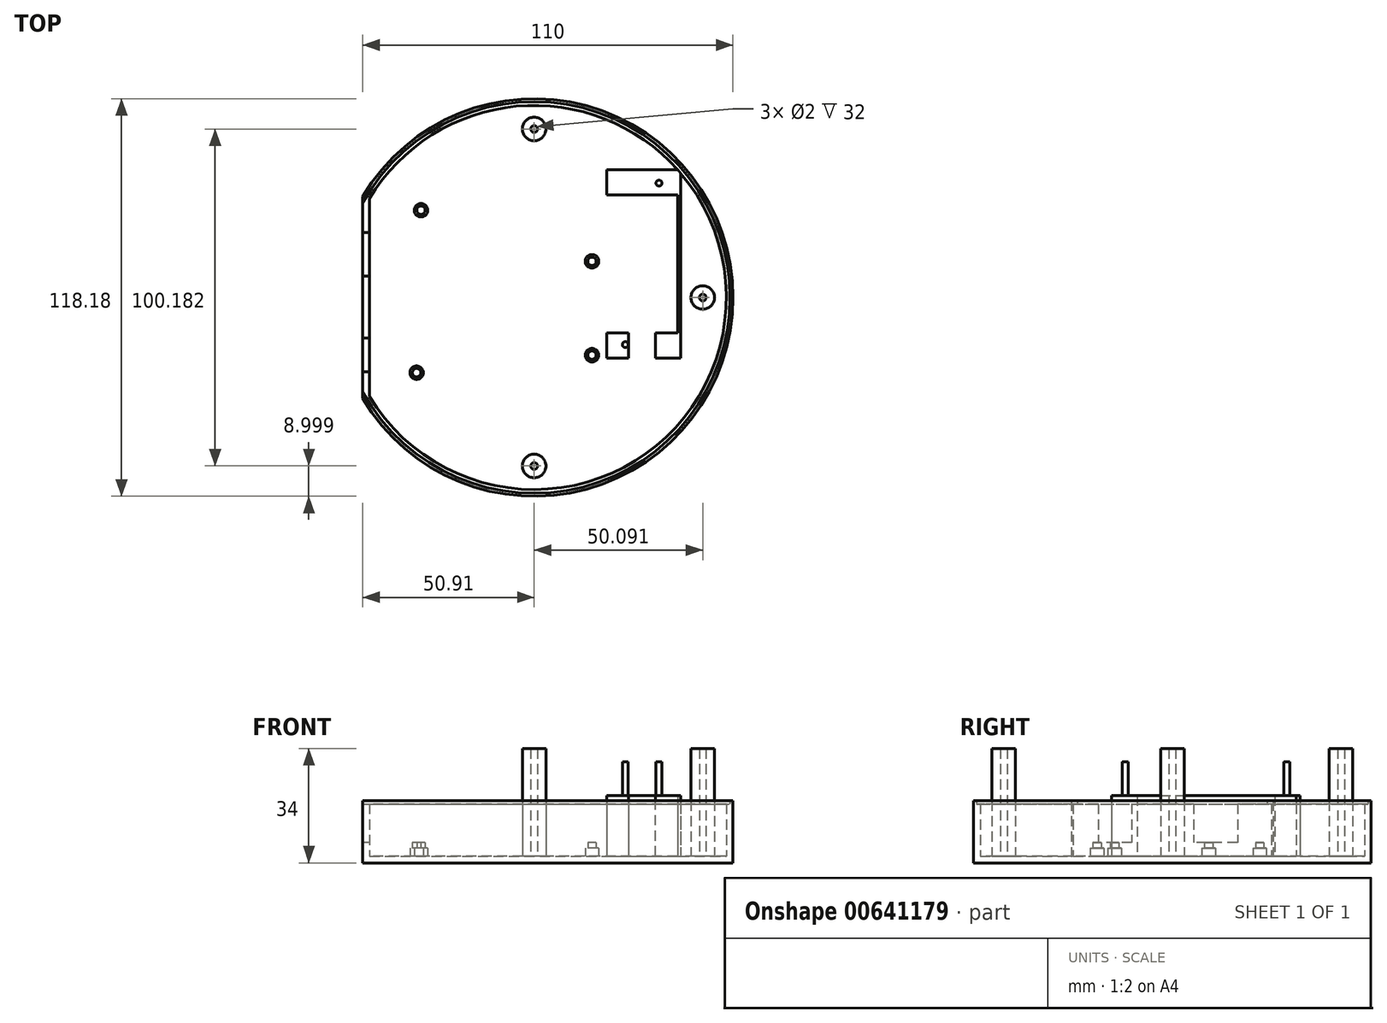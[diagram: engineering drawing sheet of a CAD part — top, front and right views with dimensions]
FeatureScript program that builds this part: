
annotation { "Feature Type Name" : "Feature", "Feature Type Description" : "" }
export const myFeature = defineFeature(function(context is Context, id is Id, definition is map)
    precondition{}
    {
        {
            var Q0;
            Q0=qCreatedBy(makeId("Top.planeOp"),FACE);
            var sketch = newSketch(context, id + "F0", { "sketchPlane" : qUnion([Q0])});
            skArc(sketch, "E0", {"start": v(-50.9, -30) * mm, "mid": v(59.1, 0) * mm, "end": v(-50.9, 30) * mm});
            skLineSegment(sketch, "E1", {"start": v(-50.9, 30) * mm, "end": v(-50.9, -30) * mm});
            skSolve(sketch);
        }
        {
            var Q0;
            Q0=makeQuery(id+"F0.imprint","IMPRINT",FACE,{"disambiguationData":[TD([[makeQuery(id+"F0.imprint","IMPRINT",EDGE,{"derivedFrom":sQuery(id+"F0.wireOp",EDGE,"E0")}),1.0]])]});
            extrude(context, id + "F1", {"entities" : qUnion([Q0]), "depth" : 2 * mm, "offsetDistance" : 25 * mm});
        }
        {
            var Q0;
            Q0=makeQuery(id+"F1.opExtrude","CAP_FACE",FACE,{"disambiguationData":[OSD([sQuery(id+"F0.wireOp",EDGE,"E0"),sQuery(id+"F0.wireOp",EDGE,"E1")])],"isStart":false});
            var sketch = newSketch(context, id + "F2", { "sketchPlane" : qUnion([Q0])});
            skArc(sketch, "E2", {"start": v(-48.9, -29.45) * mm, "mid": v(57.1, 0) * mm, "end": v(-48.9, 29.45) * mm});
            skLineSegment(sketch, "E3", {"start": v(-48.9, 29.45) * mm, "end": v(-48.9, -29.45) * mm});
            skLineSegment(sketch, "E4.bottom", {"start": v(-48.9, -24.85) * mm, "end": v(19.6, -24.85) * mm, "construction": true});
            skLineSegment(sketch, "E4.top", {"start": v(-48.9, 28.45) * mm, "end": v(19.6, 28.45) * mm, "construction": true});
            skLineSegment(sketch, "E4.left", {"start": v(-48.9, -24.85) * mm, "end": v(-48.9, 28.45) * mm, "construction": true});
            skLineSegment(sketch, "E4.right", {"start": v(19.6, -24.85) * mm, "end": v(19.6, 28.45) * mm, "construction": true});
            skLineSegment(sketch, "E5", {"start": v(-50.9, 19.35) * mm, "end": v(-48.9, 19.35) * mm});
            skLineSegment(sketch, "E6", {"start": v(-50.9, 6.35) * mm, "end": v(-48.9, 6.35) * mm});
            skLineSegment(sketch, "E7", {"start": v(-50.9, -12.05) * mm, "end": v(-48.9, -12.05) * mm});
            skLineSegment(sketch, "E8", {"start": v(-50.9, -22.05) * mm, "end": v(-48.9, -22.05) * mm});
            skCircle(sketch, "E9", {"center": v(-34.9, -22.35) * mm, "radius": 2 * mm});
            skCircle(sketch, "E10", {"center": v(-33.6, 25.95) * mm, "radius": 2 * mm});
            skCircle(sketch, "E11", {"center": v(17.2, 10.75) * mm, "radius": 2 * mm});
            skLineSegment(sketch, "E12", {"start": v(17.2, 10.75) * mm, "end": v(17.2, -19.32) * mm, "construction": true});
            skCircle(sketch, "E13", {"center": v(17.2, -17.15) * mm, "radius": 2 * mm});
            skCircle(sketch, "E14", {"center": v(-33.6, 25.95) * mm, "radius": 1.25 * mm});
            skCircle(sketch, "E15", {"center": v(-34.9, -22.35) * mm, "radius": 1.25 * mm});
            skCircle(sketch, "E16", {"center": v(17.2, 10.75) * mm, "radius": 1.25 * mm});
            skCircle(sketch, "E17", {"center": v(17.2, -17.15) * mm, "radius": 1.25 * mm});
            skSolve(sketch);
        }
        {
            var Q0;
            {var subQ2=sQuery(id+"F2.wireOp",EDGE,"E2");Q0=makeQuery(id+"F2.imprint","IMPRINT",FACE,{"disambiguationData":[TD([[makeQuery(id+"F2.imprint","IMPRINT",EDGE,{"derivedFrom":subQ2}),-1.0]])]});}
            var Q1;
            {var subQ0=sQuery(id+"F2.wireOp",EDGE,"E6");Q1=makeQuery(id+"F2.imprint","IMPRINT",FACE,{"disambiguationData":[TD([[makeQuery(id+"F2.imprint","IMPRINT",EDGE,{"derivedFrom":subQ0}),-1.0]])]});}
            var Q2;
            {var subQ0=sQuery(id+"F2.wireOp",EDGE,"E5");Q2=makeQuery(id+"F2.imprint","IMPRINT",FACE,{"disambiguationData":[TD([[makeQuery(id+"F2.imprint","IMPRINT",EDGE,{"derivedFrom":subQ0}),-1.0]])]});}
            var Q3;
            {var subQ0=sQuery(id+"F2.wireOp",EDGE,"E7");Q3=makeQuery(id+"F2.imprint","IMPRINT",FACE,{"disambiguationData":[TD([[makeQuery(id+"F2.imprint","IMPRINT",EDGE,{"derivedFrom":subQ0}),-1.0]])]});}
            extrude(context, id + "F3", {"entities" : qUnion([Q0, Q1, Q2, Q3]), "operationType" : NewBodyOperationType.ADD, "depth" : 4 * mm, "offsetDistance" : 25 * mm});
        }
        {
            var Q0;
            Q0=makeQuery(id+"F2.imprint","IMPRINT",FACE,{"disambiguationData":[TD([[makeQuery(id+"F2.imprint","IMPRINT",EDGE,{"derivedFrom":sQuery(id+"F2.wireOp",EDGE,"E14")}),1.0]])]});
            var Q1;
            Q1=makeQuery(id+"F2.imprint","IMPRINT",FACE,{"disambiguationData":[TD([[makeQuery(id+"F2.imprint","IMPRINT",EDGE,{"derivedFrom":sQuery(id+"F2.wireOp",EDGE,"E15")}),1.0]])]});
            var Q2;
            Q2=makeQuery(id+"F2.imprint","IMPRINT",FACE,{"disambiguationData":[TD([[makeQuery(id+"F2.imprint","IMPRINT",EDGE,{"derivedFrom":sQuery(id+"F2.wireOp",EDGE,"E16")}),1.0]])]});
            var Q3;
            Q3=makeQuery(id+"F2.imprint","IMPRINT",FACE,{"disambiguationData":[TD([[makeQuery(id+"F2.imprint","IMPRINT",EDGE,{"derivedFrom":sQuery(id+"F2.wireOp",EDGE,"E17")}),1.0]])]});
            extrude(context, id + "F4", {"entities" : qUnion([Q0, Q1, Q2, Q3]), "operationType" : NewBodyOperationType.ADD, "depth" : 4 * mm, "offsetDistance" : 25 * mm});
        }
        {
            var Q0;
            Q0=makeQuery(id+"F2.imprint","IMPRINT",FACE,{"disambiguationData":[TD([[makeQuery(id+"F2.imprint","IMPRINT",EDGE,{"derivedFrom":sQuery(id+"F2.wireOp",EDGE,"E10")}),1.0]])]});
            var Q1;
            Q1=makeQuery(id+"F2.imprint","IMPRINT",FACE,{"disambiguationData":[TD([[makeQuery(id+"F2.imprint","IMPRINT",EDGE,{"derivedFrom":sQuery(id+"F2.wireOp",EDGE,"E9")}),1.0]])]});
            var Q2;
            Q2=makeQuery(id+"F2.imprint","IMPRINT",FACE,{"disambiguationData":[TD([[makeQuery(id+"F2.imprint","IMPRINT",EDGE,{"derivedFrom":sQuery(id+"F2.wireOp",EDGE,"E13")}),1.0]])]});
            var Q3;
            Q3=makeQuery(id+"F2.imprint","IMPRINT",FACE,{"disambiguationData":[TD([[makeQuery(id+"F2.imprint","IMPRINT",EDGE,{"derivedFrom":sQuery(id+"F2.wireOp",EDGE,"E11")}),1.0]])]});
            extrude(context, id + "F5", {"entities" : qUnion([Q0, Q1, Q2, Q3]), "operationType" : NewBodyOperationType.ADD, "depth" : 2.4 * mm, "offsetDistance" : 25 * mm});
        }
        {
            var Q0;
            {var subQ2=sQuery(id+"F2.wireOp",EDGE,"E2");Q0=makeQuery(id+"F2.imprint","IMPRINT",FACE,{"disambiguationData":[TD([[makeQuery(id+"F2.imprint","IMPRINT",EDGE,{"derivedFrom":subQ2}),-1.0]])]});}
            var Q1;
            {var subQ0=sQuery(id+"F2.wireOp",EDGE,"E6");Q1=makeQuery(id+"F2.imprint","IMPRINT",FACE,{"disambiguationData":[TD([[makeQuery(id+"F2.imprint","IMPRINT",EDGE,{"derivedFrom":subQ0}),-1.0]])]});}
            extrude(context, id + "F6", {"entities" : qUnion([Q0, Q1]), "operationType" : NewBodyOperationType.ADD, "depth" : 15.5 * mm, "offsetDistance" : 25 * mm});
        }
        {
            var Q0;
            {var subQ4=sQuery(id+"F2.wireOp",EDGE,"E2");Q0=makeQuery(id+"F2.imprint","IMPRINT",FACE,{"disambiguationData":[TD([[makeQuery(id+"F2.imprint","IMPRINT",EDGE,{"derivedFrom":subQ4}),1.0]])]});}
            var sketch = newSketch(context, id + "F7", { "sketchPlane" : qUnion([Q0])});
            skCircle(sketch, "E18", {"center": v(50.1, 0) * mm, "radius": 3.5 * mm});
            skCircle(sketch, "E19", {"center": v(0, 50.1) * mm, "radius": 3.5 * mm});
            skCircle(sketch, "E20", {"center": v(0, -50.1) * mm, "radius": 3.5 * mm});
            skCircle(sketch, "E21", {"center": v(0, -50.1) * mm, "radius": 1 * mm});
            skCircle(sketch, "E22", {"center": v(0, 50.1) * mm, "radius": 1 * mm});
            skCircle(sketch, "E23", {"center": v(50.1, 0) * mm, "radius": 1 * mm});
            skSolve(sketch);
        }
        {
            var Q0;
            Q0=makeQuery(id+"F7.imprint","IMPRINT",FACE,{"disambiguationData":[TD([[makeQuery(id+"F7.imprint","IMPRINT",EDGE,{"derivedFrom":sQuery(id+"F7.wireOp",EDGE,"E19")}),1.0]])]});
            var Q1;
            Q1=makeQuery(id+"F7.imprint","IMPRINT",FACE,{"disambiguationData":[TD([[makeQuery(id+"F7.imprint","IMPRINT",EDGE,{"derivedFrom":sQuery(id+"F7.wireOp",EDGE,"E18")}),1.0]])]});
            var Q2;
            Q2=makeQuery(id+"F7.imprint","IMPRINT",FACE,{"disambiguationData":[TD([[makeQuery(id+"F7.imprint","IMPRINT",EDGE,{"derivedFrom":sQuery(id+"F7.wireOp",EDGE,"E20")}),1.0]])]});
            extrude(context, id + "F8", {"entities" : qUnion([Q0, Q1, Q2]), "operationType" : NewBodyOperationType.ADD, "depth" : 32 * mm, "offsetDistance" : 25 * mm});
        }
        {
            var Q0;
            {var subQ4=sQuery(id+"F2.wireOp",EDGE,"E2");Q0=makeQuery(id+"F2.imprint","IMPRINT",FACE,{"disambiguationData":[TD([[makeQuery(id+"F2.imprint","IMPRINT",EDGE,{"derivedFrom":subQ4}),1.0]])]});}
            var sketch = newSketch(context, id + "F9", { "sketchPlane" : qUnion([Q0])});
            skLineSegment(sketch, "E24", {"start": v(21.6, 38) * mm, "end": v(21.6, 30.5) * mm});
            skLineSegment(sketch, "E25", {"start": v(21.6, 30.5) * mm, "end": v(42.6, 30.5) * mm});
            skLineSegment(sketch, "E26", {"start": v(42.6, 30.5) * mm, "end": v(42.6, -10.5) * mm});
            skLineSegment(sketch, "E27", {"start": v(42.6, -10.5) * mm, "end": v(21.6, -10.5) * mm});
            skLineSegment(sketch, "E28", {"start": v(21.6, -10.5) * mm, "end": v(21.6, -18) * mm});
            skLineSegment(sketch, "E29", {"start": v(21.6, -18) * mm, "end": v(43.6, -18) * mm});
            skLineSegment(sketch, "E30", {"start": v(43.6, -18) * mm, "end": v(43.6, 38) * mm});
            skLineSegment(sketch, "E31", {"start": v(43.6, 38) * mm, "end": v(21.6, 38) * mm});
            skSolve(sketch);
        }
        {
            var Q0;
            Q0=makeQuery(id+"F9.imprint","IMPRINT",FACE,{"disambiguationData":[TD([[makeQuery(id+"F9.imprint","IMPRINT",EDGE,{"derivedFrom":sQuery(id+"F9.wireOp",EDGE,"E24")}),1.0]])]});
            extrude(context, id + "F10", {"entities" : qUnion([Q0]), "operationType" : NewBodyOperationType.ADD, "depth" : 28 * mm, "offsetDistance" : 25 * mm});
        }
        {
            var Q0;
            Q0=makeQuery(id+"F10.opExtrude","CAP_FACE",FACE,{"disambiguationData":[OSD([sQuery(id+"F9.wireOp",EDGE,"E24"),sQuery(id+"F9.wireOp",EDGE,"E25"),sQuery(id+"F9.wireOp",EDGE,"E26"),sQuery(id+"F9.wireOp",EDGE,"E27"),sQuery(id+"F9.wireOp",EDGE,"E28"),sQuery(id+"F9.wireOp",EDGE,"E29"),sQuery(id+"F9.wireOp",EDGE,"E30"),sQuery(id+"F9.wireOp",EDGE,"E31")])],"isStart":false});
            var sketch = newSketch(context, id + "F11", { "sketchPlane" : qUnion([Q0])});
            skCircle(sketch, "E32", {"center": v(27.1, 34) * mm, "radius": 0.88 * mm});
            skLineSegment(sketch, "E33", {"start": v(20.36, 10) * mm, "end": v(37.61, 10) * mm, "construction": true});
            skLineSegment(sketch, "E34", {"start": v(32.1, 16) * mm, "end": v(32.1, -15.66) * mm, "construction": true});
            skCircle(sketch, "E35.MirrorC", {"center": v(37.1, 34) * mm, "radius": 0.88 * mm});
            skCircle(sketch, "E36.MirrorC", {"center": v(37.1, -14) * mm, "radius": 0.88 * mm});
            skCircle(sketch, "E37.MirrorC", {"center": v(27.1, -14) * mm, "radius": 0.88 * mm});
            skSolve(sketch);
        }
        {
            var Q0;
            Q0=makeQuery(id+"F11.imprint","IMPRINT",FACE,{"disambiguationData":[TD([[makeQuery(id+"F11.imprint","IMPRINT",EDGE,{"derivedFrom":sQuery(id+"F11.wireOp",EDGE,"E32")}),1.0]])]});
            var Q1;
            Q1=makeQuery(id+"F11.imprint","IMPRINT",FACE,{"disambiguationData":[TD([[makeQuery(id+"F11.imprint","IMPRINT",EDGE,{"derivedFrom":sQuery(id+"F11.wireOp",EDGE,"E35.MirrorC")}),-1.0]])]});
            var Q2;
            Q2=makeQuery(id+"F11.imprint","IMPRINT",FACE,{"disambiguationData":[TD([[makeQuery(id+"F11.imprint","IMPRINT",EDGE,{"derivedFrom":sQuery(id+"F11.wireOp",EDGE,"E37.MirrorC")}),-1.0]])]});
            var Q3;
            Q3=makeQuery(id+"F11.imprint","IMPRINT",FACE,{"disambiguationData":[TD([[makeQuery(id+"F11.imprint","IMPRINT",EDGE,{"derivedFrom":sQuery(id+"F11.wireOp",EDGE,"E36.MirrorC")}),1.0]])]});
            extrude(context, id + "F12", {"entities" : qUnion([Q0, Q1, Q2, Q3]), "operationType" : NewBodyOperationType.REMOVE, "oppositeDirection" : true, "depth" : 10 * mm, "offsetDistance" : 25 * mm});
        }
        {
            var Q0;
            Q0=makeQuery(id+"F10.opExtrude","SWEPT_FACE",FACE,{"disambiguationData":[OSD([sQuery(id+"F9.wireOp",EDGE,"E29")])]});
            var sketch = newSketch(context, id + "F13", { "sketchPlane" : qUnion([Q0])});
            skLineSegment(sketch, "E38.0", {"start": v(21.6, 30) * mm, "end": v(43.6, 30) * mm, "construction": true});
            skLineSegment(sketch, "E39.0", {"start": v(21.6, 30) * mm, "end": v(21.6, 2) * mm, "construction": true});
            skLineSegment(sketch, "E40.0", {"start": v(43.6, 30) * mm, "end": v(43.6, 2) * mm, "construction": true});
            skLineSegment(sketch, "E41", {"start": v(30.1, 30) * mm, "end": v(30.1, 23) * mm});
            skLineSegment(sketch, "E42", {"start": v(30.1, 23) * mm, "end": v(28.1, 21) * mm});
            skLineSegment(sketch, "E43", {"start": v(28.1, 21) * mm, "end": v(28.1, 2) * mm});
            skLineSegment(sketch, "E44", {"start": v(28.1, 2) * mm, "end": v(36.1, 2) * mm});
            skLineSegment(sketch, "E45", {"start": v(36.1, 2) * mm, "end": v(36.1, 21) * mm});
            skLineSegment(sketch, "E46", {"start": v(36.1, 21) * mm, "end": v(34.1, 23) * mm});
            skLineSegment(sketch, "E47", {"start": v(34.1, 23) * mm, "end": v(34.1, 30) * mm});
            skLineSegment(sketch, "E48", {"start": v(34.1, 30) * mm, "end": v(30.1, 30) * mm});
            skSolve(sketch);
        }
        {
            var Q0;
            Q0 = qSketchRegion(id + "F13", true);
            extrude(context, id + "F14", {"entities" : qUnion([Q0]), "operationType" : NewBodyOperationType.REMOVE, "oppositeDirection" : true, "depth" : 25 * mm, "offsetDistance" : 25 * mm});
        }
        {
            var Q0;
            Q0=makeQuery(id+"F6.opExtrude","CAP_FACE",FACE,{"disambiguationData":[OSD([sQuery(id+"F0.wireOp",EDGE,"E0"),sQuery(id+"F0.wireOp",EDGE,"E1"),sQuery(id+"F2.wireOp",EDGE,"E2"),sQuery(id+"F2.wireOp",EDGE,"E3"),sQuery(id+"F2.wireOp",EDGE,"E5"),sQuery(id+"F2.wireOp",EDGE,"E8")])],"isStart":false});
            var sketch = newSketch(context, id + "F15", { "sketchPlane" : qUnion([Q0])});
            skArc(sketch, "E49.0", {"start": v(-50.9, -30) * mm, "mid": v(59.1, 0) * mm, "end": v(-50.9, 30) * mm, "construction": true});
            skPoint(sketch, "E50.0", {"position": v(-50.9, 24.67) * mm});
            skLineSegment(sketch, "E51.0", {"start": v(-50.9, 6.35) * mm, "end": v(-50.9, -12.05) * mm, "construction": true});
            skArc(sketch, "E52", {"start": v(-50.9, -30) * mm, "mid": v(59.1, 0) * mm, "end": v(-50.9, 30) * mm});
            skArc(sketch, "E53", {"start": v(-50.9, -28.19) * mm, "mid": v(58.2, 0) * mm, "end": v(-50.9, 28.19) * mm});
            skLineSegment(sketch, "E54", {"start": v(-50.9, 30) * mm, "end": v(-50.9, 28.19) * mm});
            skLineSegment(sketch, "E55", {"start": v(-50.9, -30) * mm, "end": v(-50.9, -28.19) * mm});
            skSolve(sketch);
        }
        {
            var Q0;
            Q0 = qSketchRegion(id + "F15", true);
            extrude(context, id + "F16", {"entities" : qUnion([Q0]), "operationType" : NewBodyOperationType.ADD, "depth" : 1 * mm, "offsetDistance" : 25 * mm});
        }
    });
